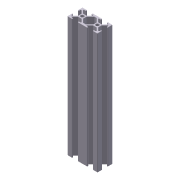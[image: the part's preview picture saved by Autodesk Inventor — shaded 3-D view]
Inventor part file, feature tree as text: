
AUTODESK INVENTOR PART (.ipt)
format: ipt  version: 2014 (Build 180170000, 170)  size: 589,312 bytes
history: native  units: mm
features: other x8, fillet x5, extrude x3, sketch x3, pattern_circular x1, mirror x1
ambient origin geometry x8: Origin, YZ Plane, XZ Plane, XY Plane, X Axis, Y Axis, Z Axis, Center Point
bodies: Solid1 (feature_tree)
feature tree (21):
  other  "Table"
  other  "Length = 50 mm"
  other  "Length = 75"
  other  "Length = 100"
  other  "Length = 150 mm"
  other  "Length = 200 mm"
  other  "Length = 250 mm"
  other  "Length = 300 mm"
  extrude  "Extrusion1"  Depth=8.76mm
  extrude  "Extrusion2"  Depth=12.5mm
  pattern_circular  "Circular Pattern1"  [2 undecoded]
  mirror  "Mirror1"
  extrude  "Extrusion3"  Depth=2.14mm
  fillet  "Fillet4"  Radius=200.0mm
  fillet  "Fillet5"  Radius=40.0mm
  fillet  "Fillet6"  Radius=10.0mm
  fillet  "Fillet7"  Radius=1.0mm
  fillet  "Fillet8"  Radius=0.75mm
  sketch  "Sketch1"  dims[d0=8.76mm d1=5.0mm]
  sketch  "Sketch2"  dims[d3=0.0mm d4=12.5mm]
  sketch  "Sketch3"  dims[d5=2.14mm d6=8.1mm d7=2.14mm d8=200.0mm d9=0.0mm d10=40.0mm d11=360.0deg d16=10.0mm d17=0.0mm d18=1.0mm d19=0.75mm d20=0.75mm d21=0.75mm d22=0.75mm]
note: 2 required parameter values undecoded (feature->parameter linkage not recoverable at this tier; creation-order binding heuristic only, values carry confidence <= 0.55)
